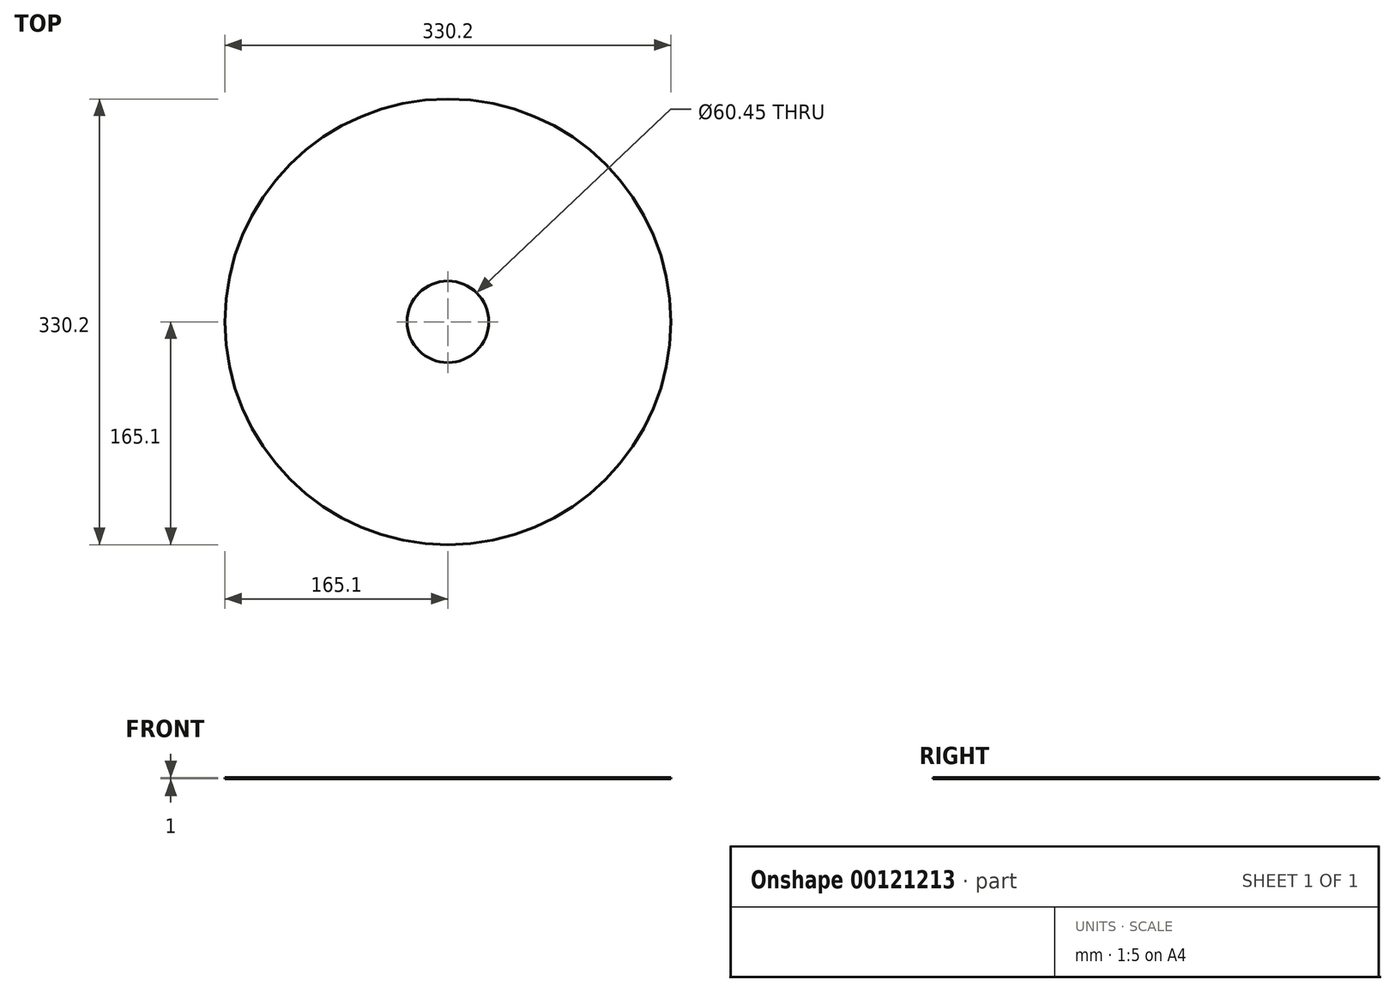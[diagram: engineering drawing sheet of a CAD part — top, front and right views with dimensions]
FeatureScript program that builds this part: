
annotation { "Feature Type Name" : "Feature", "Feature Type Description" : "" }
export const myFeature = defineFeature(function(context is Context, id is Id, definition is map)
    precondition{}
    {
        {
            var Q0;
            Q0=qCreatedBy(makeId("Top.planeOp"),FACE);
            var sketch = newSketch(context, id + "F0", { "sketchPlane" : qUnion([Q0])});
            skCircle(sketch, "E0", {"center": v(0, 0) * mm, "radius": 165.1 * mm});
            skCircle(sketch, "E1", {"center": v(0, 0) * mm, "radius": 30.23 * mm});
            skSolve(sketch);
        }
        {
            var Q0;
            Q0 = qSketchRegion(id + "F0", true);
            extrude(context, id + "F1", {"entities" : qUnion([Q0]), "depth" : 1 * mm});
        }
    });
